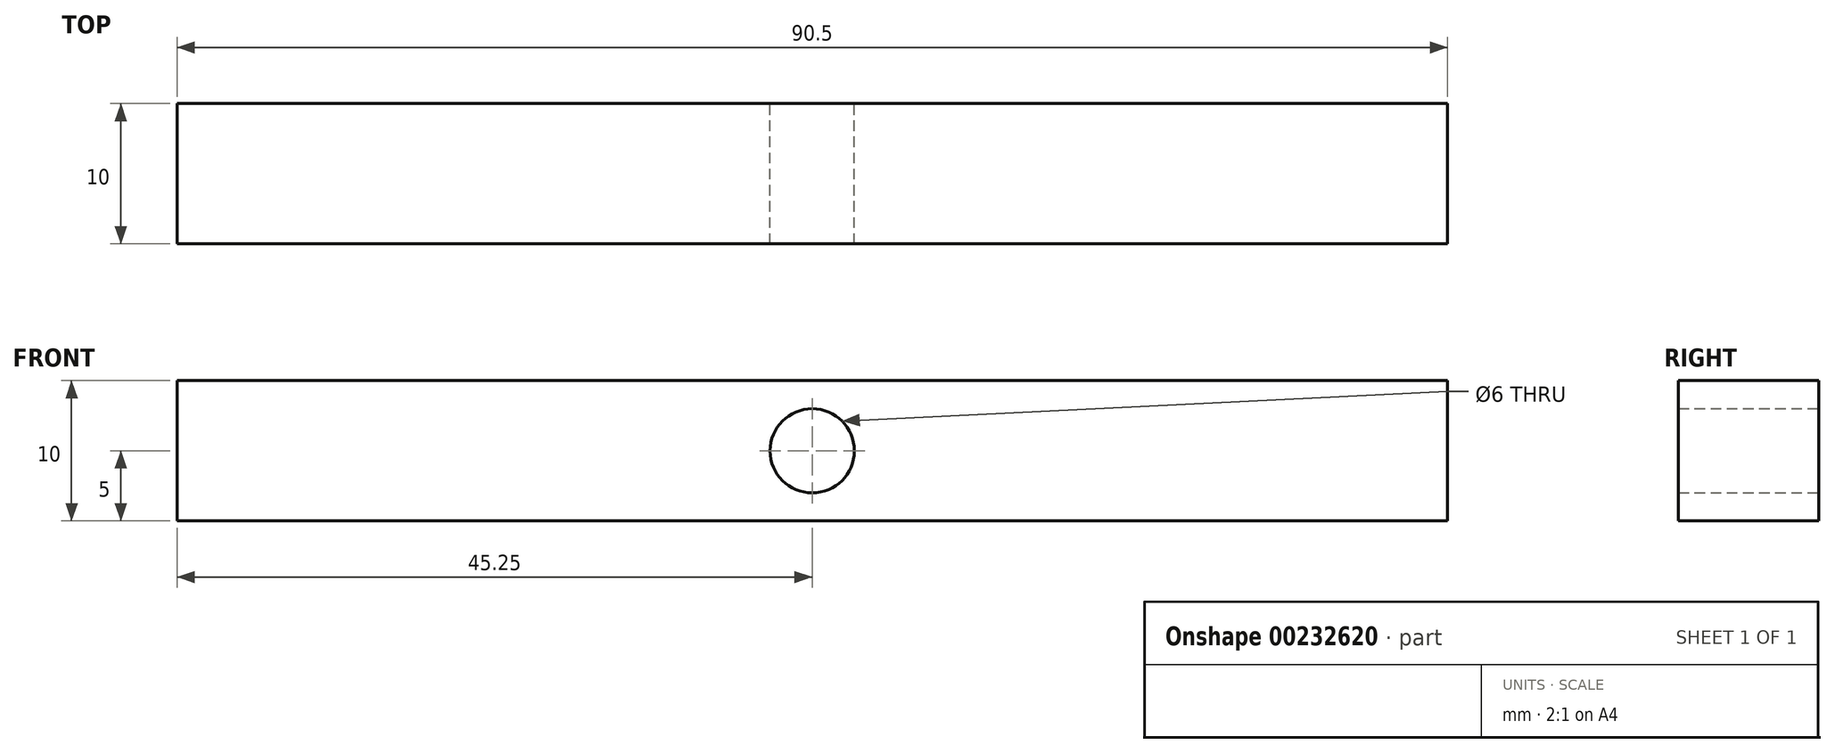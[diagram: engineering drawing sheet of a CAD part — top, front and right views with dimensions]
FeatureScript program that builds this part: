
annotation { "Feature Type Name" : "Feature", "Feature Type Description" : "" }
export const myFeature = defineFeature(function(context is Context, id is Id, definition is map)
    precondition{}
    {
        {
            var Q0;
            Q0=qCreatedBy(makeId("Front.planeOp"),FACE);
            var sketch = newSketch(context, id + "F0", { "sketchPlane" : qUnion([Q0])});
            skLineSegment(sketch, "E0.bottom", {"start": v(0, 0) * mm, "end": v(90.5, 0) * mm});
            skLineSegment(sketch, "E0.top", {"start": v(0, 10) * mm, "end": v(90.5, 10) * mm});
            skLineSegment(sketch, "E0.left", {"start": v(0, 0) * mm, "end": v(0, 10) * mm});
            skLineSegment(sketch, "E0.right", {"start": v(90.5, 0) * mm, "end": v(90.5, 10) * mm});
            skSolve(sketch);
        }
        {
            var Q0;
            Q0=makeQuery(id+"F0.imprint","IMPRINT",FACE,{"disambiguationData":[TD([[makeQuery(id+"F0.imprint","IMPRINT",EDGE,{"derivedFrom":sQuery(id+"F0.wireOp",EDGE,"E0.bottom")}),1.0]])]});
            extrude(context, id + "F1", {"entities" : qUnion([Q0]), "depth" : 10 * mm});
        }
        {
            var Q0;
            Q0=makeQuery(id+"F1.opExtrude","CAP_FACE",FACE,{"disambiguationData":[OSD([sQuery(id+"F0.wireOp",EDGE,"E0.bottom"),sQuery(id+"F0.wireOp",EDGE,"E0.top"),sQuery(id+"F0.wireOp",EDGE,"E0.left"),sQuery(id+"F0.wireOp",EDGE,"E0.right")])],"isStart":true});
            var sketch = newSketch(context, id + "F2", { "sketchPlane" : qUnion([Q0])});
            skCircle(sketch, "E1", {"center": v(-45.25, 5) * mm, "radius": 3 * mm});
            skSolve(sketch);
        }
        {
            var Q0;
            Q0 = qSketchRegion(id + "F2", true);
            extrude(context, id + "F3", {"entities" : qUnion([Q0]), "operationType" : NewBodyOperationType.REMOVE, "oppositeDirection" : true, "depth" : 25 * mm});
        }
    });
